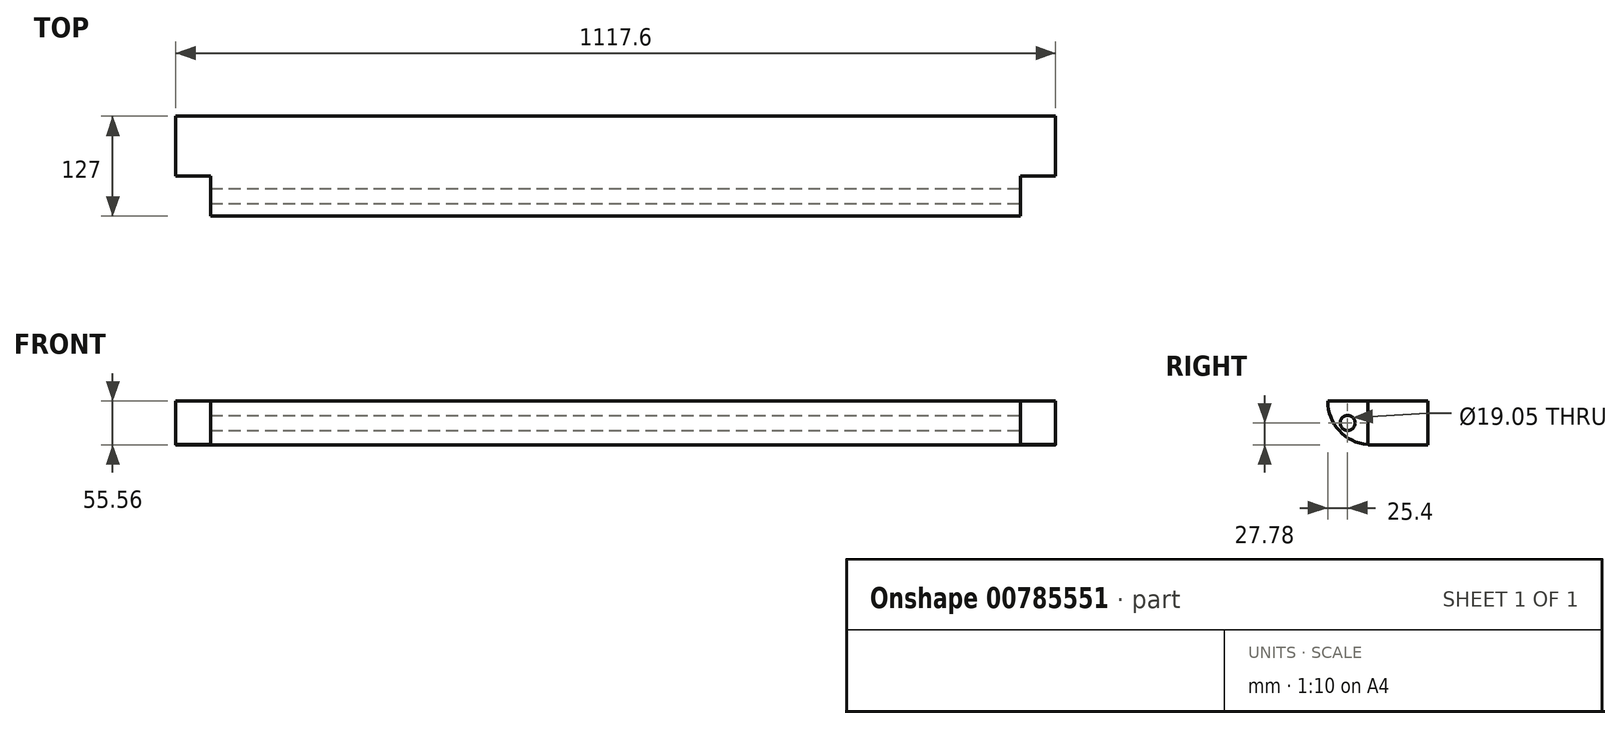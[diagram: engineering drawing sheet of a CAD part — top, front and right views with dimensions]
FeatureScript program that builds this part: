
annotation { "Feature Type Name" : "Feature", "Feature Type Description" : "" }
export const myFeature = defineFeature(function(context is Context, id is Id, definition is map)
    precondition{}
    {
        {
            var Q0;
            Q0=qCreatedBy(makeId("Right.planeOp"),FACE);
            var sketch = newSketch(context, id + "F0", { "sketchPlane" : qUnion([Q0])});
            skLineSegment(sketch, "E0.bottom", {"start": v(63.5, 27.78) * mm, "end": v(-63.5, 27.78) * mm});
            skLineSegment(sketch, "E0.top", {"start": v(63.5, -27.78) * mm, "end": v(-63.5, -27.78) * mm});
            skLineSegment(sketch, "E0.left", {"start": v(63.5, 27.78) * mm, "end": v(63.5, -27.78) * mm});
            skLineSegment(sketch, "E0.right", {"start": v(-63.5, 27.78) * mm, "end": v(-63.5, -27.78) * mm});
            skPoint(sketch, "E0.middle", {"position": v(0, 0) * mm});
            skSolve(sketch);
        }
        {
            var Q0;
            Q0 = qSketchRegion(id + "F0", true);
            extrude(context, id + "F1", {"entities" : qUnion([Q0]), "depth" : 1117.6 * mm, "offsetDistance" : 25.4 * mm});
        }
        {
            var Q0;
            Q0=makeQuery(id+"F1.opExtrude","SWEPT_FACE",FACE,{"disambiguationData":[OSD([sQuery(id+"F0.wireOp",EDGE,"E0.bottom")])]});
            var sketch = newSketch(context, id + "F2", { "sketchPlane" : qUnion([Q0])});
            skLineSegment(sketch, "E1.bottom", {"start": v(0, -63.5) * mm, "end": v(44.45, -63.5) * mm});
            skLineSegment(sketch, "E1.top", {"start": v(0, -12.7) * mm, "end": v(44.45, -12.7) * mm});
            skLineSegment(sketch, "E1.left", {"start": v(0, -63.5) * mm, "end": v(0, -12.7) * mm});
            skLineSegment(sketch, "E1.right", {"start": v(44.45, -63.5) * mm, "end": v(44.45, -12.7) * mm});
            skLineSegment(sketch, "E2", {"start": v(558.8, -63.5) * mm, "end": v(558.8, 63.5) * mm});
            skLineSegment(sketch, "E3.MirrorCS", {"start": v(1073.15, -63.5) * mm, "end": v(1073.15, -12.7) * mm});
            skLineSegment(sketch, "E4.MirrorCS", {"start": v(1117.6, -12.7) * mm, "end": v(1073.15, -12.7) * mm});
            skLineSegment(sketch, "E5.MirrorCS", {"start": v(1117.6, -63.5) * mm, "end": v(1073.15, -63.5) * mm});
            skLineSegment(sketch, "E6.MirrorCS", {"start": v(1117.6, -63.5) * mm, "end": v(1117.6, -12.7) * mm});
            skSolve(sketch);
        }
        {
            var Q0;
            Q0 = qSketchRegion(id + "F2", true);
            extrude(context, id + "F3", {"entities" : qUnion([Q0]), "operationType" : NewBodyOperationType.REMOVE, "endBound" : BoundingType.THROUGH_ALL, "oppositeDirection" : true, "depth" : 25.4 * mm, "offsetDistance" : 25.4 * mm});
        }
        {
            var Q0;
            Q0=makeQuery(id+"F3.boolean.opBoolean","COPY",FACE,{"derivedFrom":makeQuery(id+"F3.opExtrude","SWEPT_FACE",FACE,{"disambiguationData":[OSD([sQuery(id+"F2.wireOp",EDGE,"E3.MirrorCS")])]})});
            var sketch = newSketch(context, id + "F4", { "sketchPlane" : qUnion([Q0])});
            skLineSegment(sketch, "E7", {"start": v(-63.5, -27.78) * mm, "end": v(-12.7, 27.78) * mm});
            skLineSegment(sketch, "E8", {"start": v(-12.7, 27.78) * mm, "end": v(-63.5, 27.78) * mm});
            skLineSegment(sketch, "E9", {"start": v(-63.5, 27.78) * mm, "end": v(-12.7, -27.78) * mm});
            skCircle(sketch, "E10", {"center": v(-38.1, 0) * mm, "radius": 9.53 * mm});
            skSolve(sketch);
        }
        {
            var Q0;
            {var subQ0=sQuery(id+"F4.wireOp",EDGE,"E10");var subQ1=sQuery(id+"F4.wireOp",EDGE,"E7");var subQ2=makeQuery(id+"F4.imprint","INTERSECT",VERTEX,{"disambiguationData":[OD(0.0)],"derivedFrom":[subQ1,subQ0]});Q0=makeQuery(id+"F4.imprint","IMPRINT",FACE,{"disambiguationData":[TD([[makeQuery(id+"F4.imprint","IMPRINT",EDGE,{"disambiguationData":[TD([[subQ2,-1.0]])],"derivedFrom":subQ1}),-1.0]])]});}
            var Q1;
            {var subQ0=sQuery(id+"F4.wireOp",EDGE,"E10");var subQ1=sQuery(id+"F4.wireOp",EDGE,"E7");var subQ2=makeQuery(id+"F4.imprint","INTERSECT",VERTEX,{"disambiguationData":[OD(0.0)],"derivedFrom":[subQ1,subQ0]});Q1=makeQuery(id+"F4.imprint","IMPRINT",FACE,{"disambiguationData":[TD([[makeQuery(id+"F4.imprint","IMPRINT",EDGE,{"disambiguationData":[TD([[subQ2,-1.0]])],"derivedFrom":subQ1}),1.0]])]});}
            var Q2;
            {var subQ0=sQuery(id+"F4.wireOp",EDGE,"E9");var subQ1=sQuery(id+"F4.wireOp",EDGE,"E7");var subQ2=makeQuery(id+"F4.imprint","INTERSECT",VERTEX,{"derivedFrom":[subQ1,subQ0]});Q2=makeQuery(id+"F4.imprint","IMPRINT",FACE,{"disambiguationData":[TD([[makeQuery(id+"F4.imprint","IMPRINT",EDGE,{"disambiguationData":[TD([[subQ2,-1.0]])],"derivedFrom":subQ1}),1.0]])]});}
            var Q3;
            {var subQ0=sQuery(id+"F4.wireOp",EDGE,"E9");var subQ1=sQuery(id+"F4.wireOp",EDGE,"E7");var subQ2=makeQuery(id+"F4.imprint","INTERSECT",VERTEX,{"derivedFrom":[subQ1,subQ0]});Q3=makeQuery(id+"F4.imprint","IMPRINT",FACE,{"disambiguationData":[TD([[makeQuery(id+"F4.imprint","IMPRINT",EDGE,{"disambiguationData":[TD([[subQ2,-1.0]])],"derivedFrom":subQ1}),-1.0]])]});}
            extrude(context, id + "F5", {"entities" : qUnion([Q0, Q1, Q2, Q3]), "operationType" : NewBodyOperationType.REMOVE, "endBound" : BoundingType.THROUGH_ALL, "oppositeDirection" : true, "depth" : 25.4 * mm, "offsetDistance" : 25.4 * mm});
        }
        {
            var Q0;
            Q0=makeQuery(id+"F1.opExtrude","SWEPT_EDGE",EDGE,{"disambiguationData":[OSD([sQuery(id+"F0.wireOp",EDGE,"E0.top"),sQuery(id+"F0.wireOp",EDGE,"E0.right")])]});
            fillet(context, id + "F6", {"entities" : qUnion([Q0]), "radius" : 55.56 * mm, "tangentPropagation" : true, "allowEdgeOverflow" : false});
        }
    });
